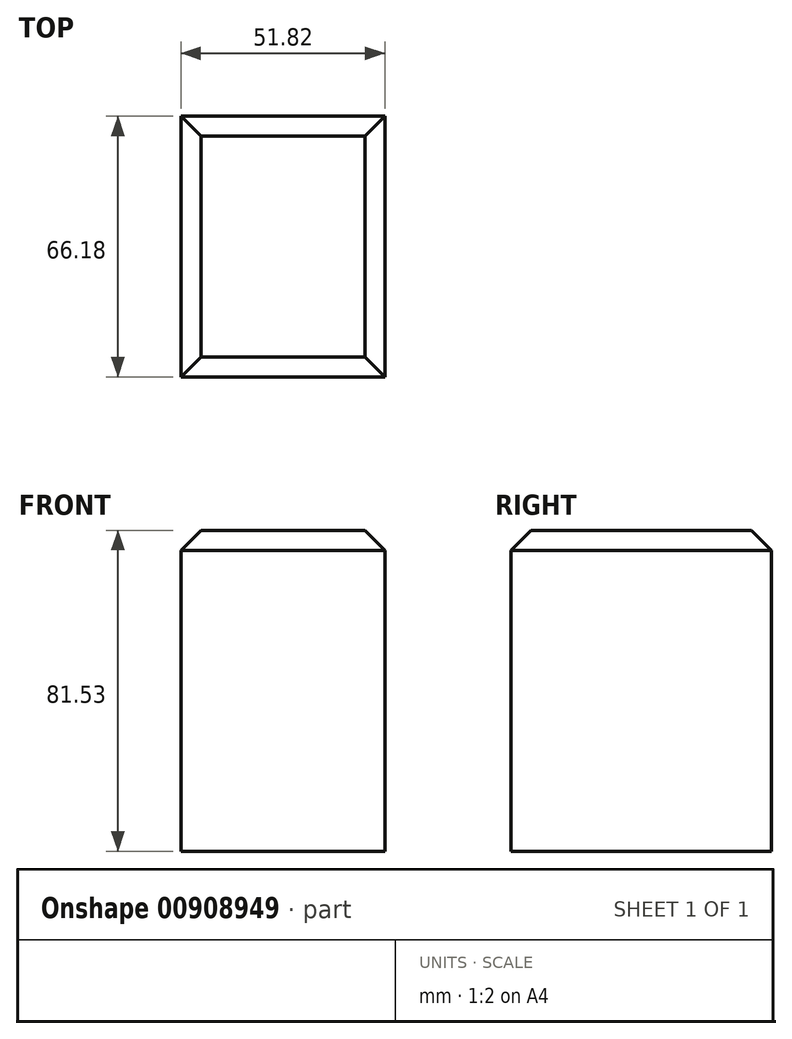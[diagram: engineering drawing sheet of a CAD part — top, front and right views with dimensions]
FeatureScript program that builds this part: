
annotation { "Feature Type Name" : "Feature", "Feature Type Description" : "" }
export const myFeature = defineFeature(function(context is Context, id is Id, definition is map)
    precondition{}
    {
        {
            var Q0;
            Q0=qCreatedBy(makeId("Top.planeOp"),FACE);
            var sketch = newSketch(context, id + "F0", { "sketchPlane" : qUnion([Q0])});
            skLineSegment(sketch, "E0.bottom", {"start": v(-25.9, -33.1) * mm, "end": v(25.9, -33.1) * mm});
            skLineSegment(sketch, "E0.top", {"start": v(-25.9, 33.1) * mm, "end": v(25.9, 33.1) * mm});
            skLineSegment(sketch, "E0.left", {"start": v(-25.9, -33.1) * mm, "end": v(-25.9, 33.1) * mm});
            skLineSegment(sketch, "E0.right", {"start": v(25.9, -33.1) * mm, "end": v(25.9, 33.1) * mm});
            skPoint(sketch, "E0.middle", {"position": v(0, 0) * mm});
            skSolve(sketch);
        }
        {
            var Q0;
            Q0=makeQuery(id+"F0.imprint","IMPRINT",FACE,{"disambiguationData":[TD([[makeQuery(id+"F0.imprint","IMPRINT",EDGE,{"derivedFrom":sQuery(id+"F0.wireOp",EDGE,"E0.bottom")}),1.0]])]});
            extrude(context, id + "F1", {"entities" : qUnion([Q0]), "depth" : 81.53 * mm, "offsetDistance" : 25.4 * mm});
        }
        {
            var Q0;
            Q0=makeQuery(id+"F1.opExtrude","CAP_EDGE",EDGE,{"disambiguationData":[OSD([sQuery(id+"F0.wireOp",EDGE,"E0.bottom")])],"isStart":false});
            var Q1;
            Q1=makeQuery(id+"F1.opExtrude","CAP_EDGE",EDGE,{"disambiguationData":[OSD([sQuery(id+"F0.wireOp",EDGE,"E0.right")])],"isStart":false});
            var Q2;
            Q2=makeQuery(id+"F1.opExtrude","CAP_EDGE",EDGE,{"disambiguationData":[OSD([sQuery(id+"F0.wireOp",EDGE,"E0.top")])],"isStart":false});
            var Q3;
            Q3=makeQuery(id+"F1.opExtrude","CAP_EDGE",EDGE,{"disambiguationData":[OSD([sQuery(id+"F0.wireOp",EDGE,"E0.left")])],"isStart":false});
            chamfer(context, id + "F2", {"entities" : qUnion([Q0, Q1, Q2, Q3]), "width" : 5.08 * mm, "tangentPropagation" : true});
        }
    });
